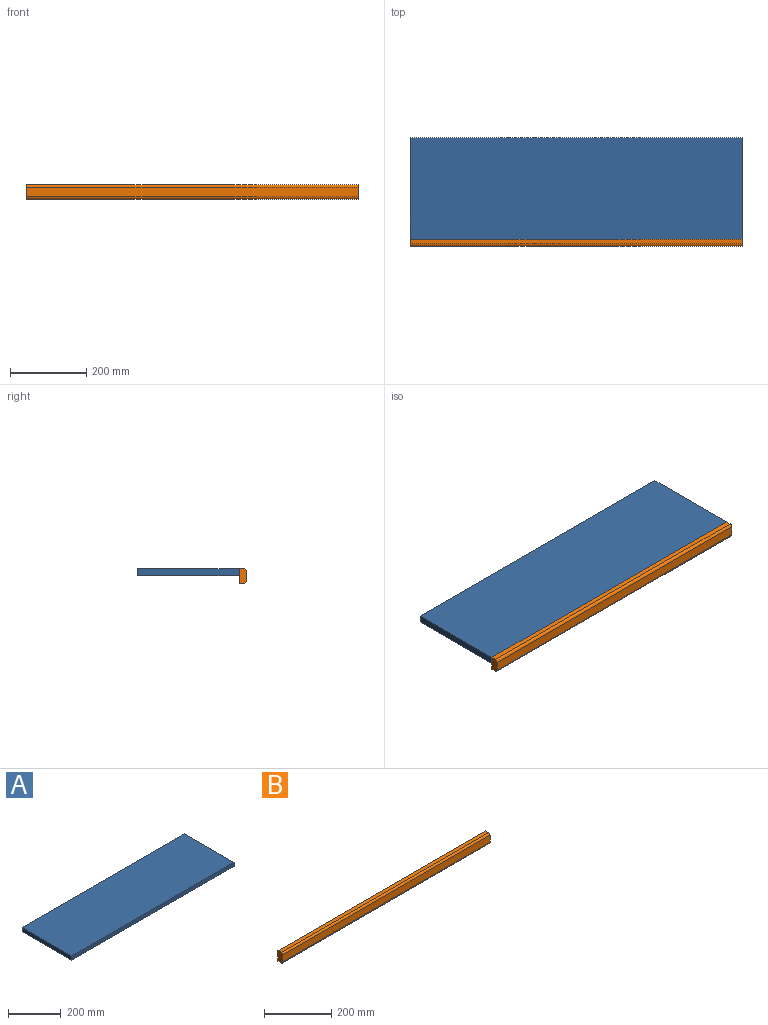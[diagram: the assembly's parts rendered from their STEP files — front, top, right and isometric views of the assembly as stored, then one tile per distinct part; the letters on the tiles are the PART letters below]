
ASSEMBLY  parts=2 mates=1
PART A: 6 faces, bbox 873.1x266.7x19.1 mm
  f0: plane 266.7x19.05mm, normal (1,0,0), area 5080.6mm2, adj f1,f3,f4,f5
  f1: plane 873.13x19.05mm, normal (0,1,0), area 16633mm2, adj f0,f2,f4,f5
  f2: plane 266.7x19.05mm, normal (-1,0,0), area 5080.6mm2, adj f1,f3,f4,f5
  f3: plane 873.13x19.05mm, normal (0,-1,0), area 16633mm2, adj f0,f2,f4,f5
  f4: plane 873.13x266.7mm, normal (0,0,1), area 232862.4mm2, adj f0,f1,f2,f3
  f5: plane 873.13x266.7mm, normal (0,0,-1), area 232862.4mm2, adj f0,f1,f2,f3
PART B: 8 faces, bbox 873.1x19.1x38.1 mm
  f0: plane 38.1x19.05mm, normal (1,0,0), area 708.5mm2, adj f1,f3,f4,f5,f6,f7
  f1: plane 873.13x12.7mm, normal (0,0,1), area 11088.7mm2, adj f0,f2,f5,f6
  f2: plane 38.1x19.05mm, normal (-1,0,0), area 708.5mm2, adj f1,f3,f4,f5,f6,f7
  f3: plane 873.13x12.7mm, normal (0,0,-1), area 11088.7mm2, adj f0,f2,f5,f7
  f4: plane 873.13x25.4mm, normal (0,-1,0), area 22177.4mm2, adj f0,f2,f6,f7
  f5: plane 873.13x38.1mm, normal (0,1,0), area 33266.1mm2, adj f0,f1,f2,f3
  f6: cylinder r=6.35mm len=873.13mm, axis (1,0,0), area 8709mm2, adj f0,f1,f2,f4
  f7: cylinder r=6.35mm len=873.13mm, axis (-1,0,0), area 8709mm2, adj f0,f2,f3,f4
PLACE A t=(436.56,133.35,0)mm
PLACE B t=(436.56,0,0)mm
MATE fastened B.f5 <-> A.f3  axis (0,1,0) through (873.12,0,19.05)mm
